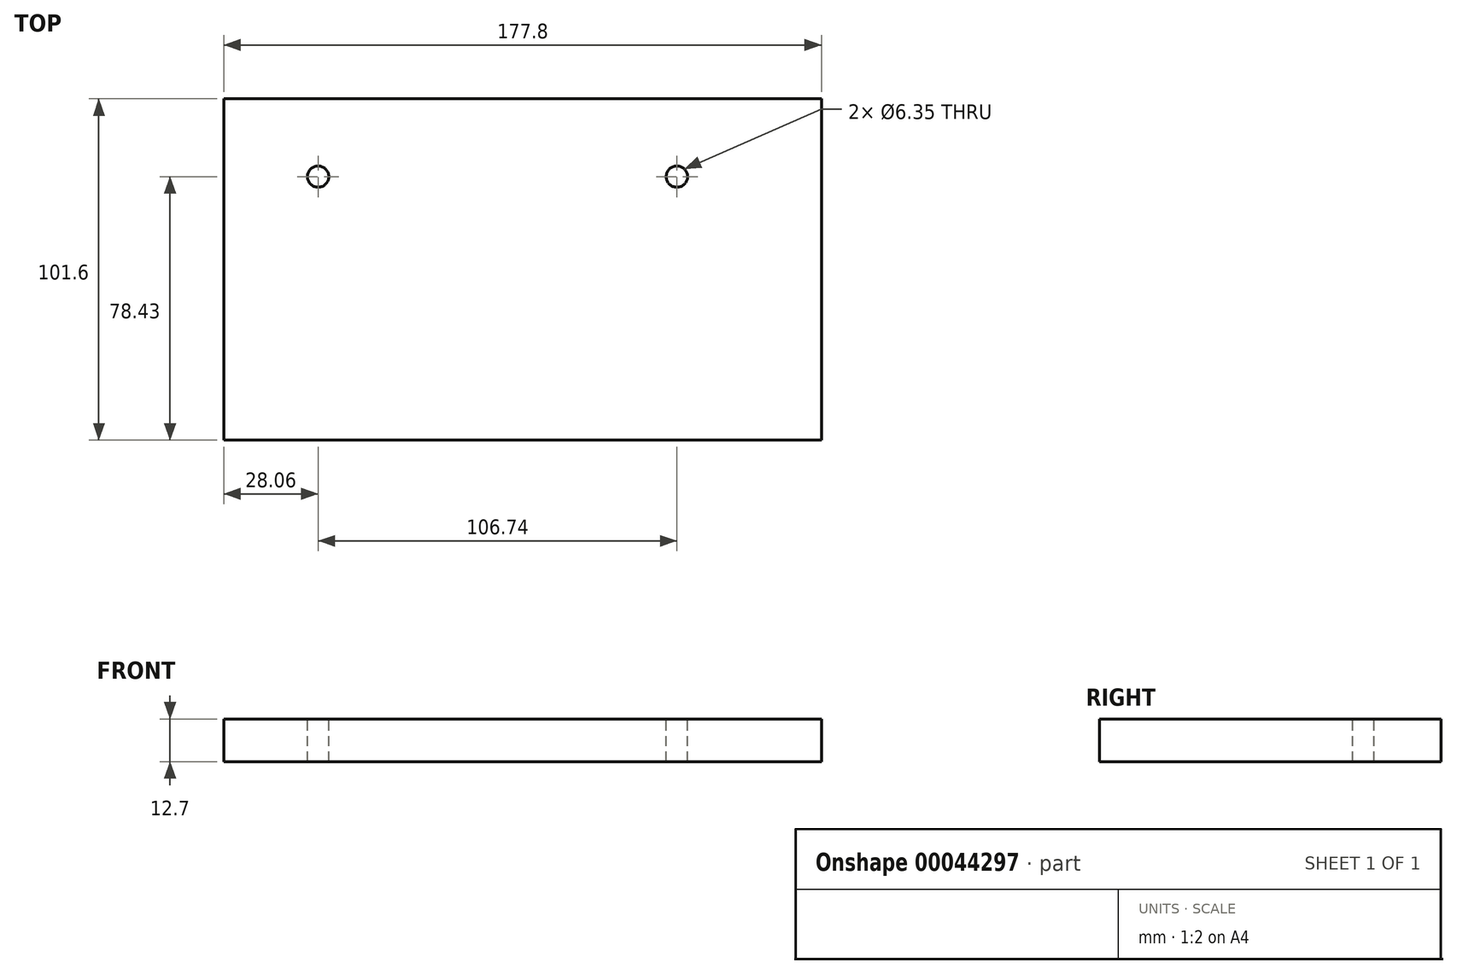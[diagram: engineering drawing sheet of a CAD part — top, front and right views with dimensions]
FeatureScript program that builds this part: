
annotation { "Feature Type Name" : "Feature", "Feature Type Description" : "" }
export const myFeature = defineFeature(function(context is Context, id is Id, definition is map)
    precondition{}
    {
        {
            var Q0;
            Q0=qCreatedBy(makeId("Top.planeOp"),FACE);
            var sketch = newSketch(context, id + "F0", { "sketchPlane" : qUnion([Q0])});
            skLineSegment(sketch, "E0.bottom", {"start": v(-88.9, 50.8) * mm, "end": v(88.9, 50.8) * mm});
            skLineSegment(sketch, "E0.top", {"start": v(-88.9, -50.8) * mm, "end": v(88.9, -50.8) * mm});
            skLineSegment(sketch, "E0.left", {"start": v(-88.9, 50.8) * mm, "end": v(-88.9, -50.8) * mm});
            skLineSegment(sketch, "E0.right", {"start": v(88.9, 50.8) * mm, "end": v(88.9, -50.8) * mm});
            skSolve(sketch);
        }
        {
            var Q0;
            Q0=makeQuery(id+"F0.imprint","IMPRINT",FACE,{"disambiguationData":[TD([[makeQuery(id+"F0.imprint","IMPRINT",EDGE,{"derivedFrom":sQuery(id+"F0.wireOp",EDGE,"E0.bottom")}),-1.0]])]});
            extrude(context, id + "F1", {"entities" : qUnion([Q0]), "depth" : 12.7 * mm});
        }
        {
            var Q0;
            Q0=makeQuery(id+"F1.opExtrude","CAP_FACE",FACE,{"disambiguationData":[OSD([sQuery(id+"F0.wireOp",EDGE,"E0.bottom"),sQuery(id+"F0.wireOp",EDGE,"E0.top"),sQuery(id+"F0.wireOp",EDGE,"E0.left"),sQuery(id+"F0.wireOp",EDGE,"E0.right")])],"isStart":false});
            var sketch = newSketch(context, id + "F2", { "sketchPlane" : qUnion([Q0])});
            skCircle(sketch, "E1", {"center": v(-60.84, 27.63) * mm, "radius": 2.95 * mm});
            skCircle(sketch, "E2", {"center": v(45.9, 27.63) * mm, "radius": 3.22 * mm});
            skSolve(sketch);
        }
        {
            var Q0;
            Q0=sQuery(id+"F2.wireOp",VERTEX,"E2.center");
            var Q1;
            Q1=sQuery(id+"F2.wireOp",VERTEX,"E1.center");
            var Q2;
            Q2=makeQuery(id+"F1.opExtrude","SWEPT_BODY",BODY,{"disambiguationData":[OSD([sQuery(id+"F0.wireOp",EDGE,"E0.bottom"),sQuery(id+"F0.wireOp",EDGE,"E0.top"),sQuery(id+"F0.wireOp",EDGE,"E0.left"),sQuery(id+"F0.wireOp",EDGE,"E0.right")])]});
            hole(context, id + "F3", {"style" : HoleStyle.SIMPLE, "holeDiameter" : 6.35 * mm, "endStyle" : HoleEndStyle.THROUGH, "locations" : qUnion([Q0, Q1]), "scope" : qUnion([Q2])});
        }
    });
